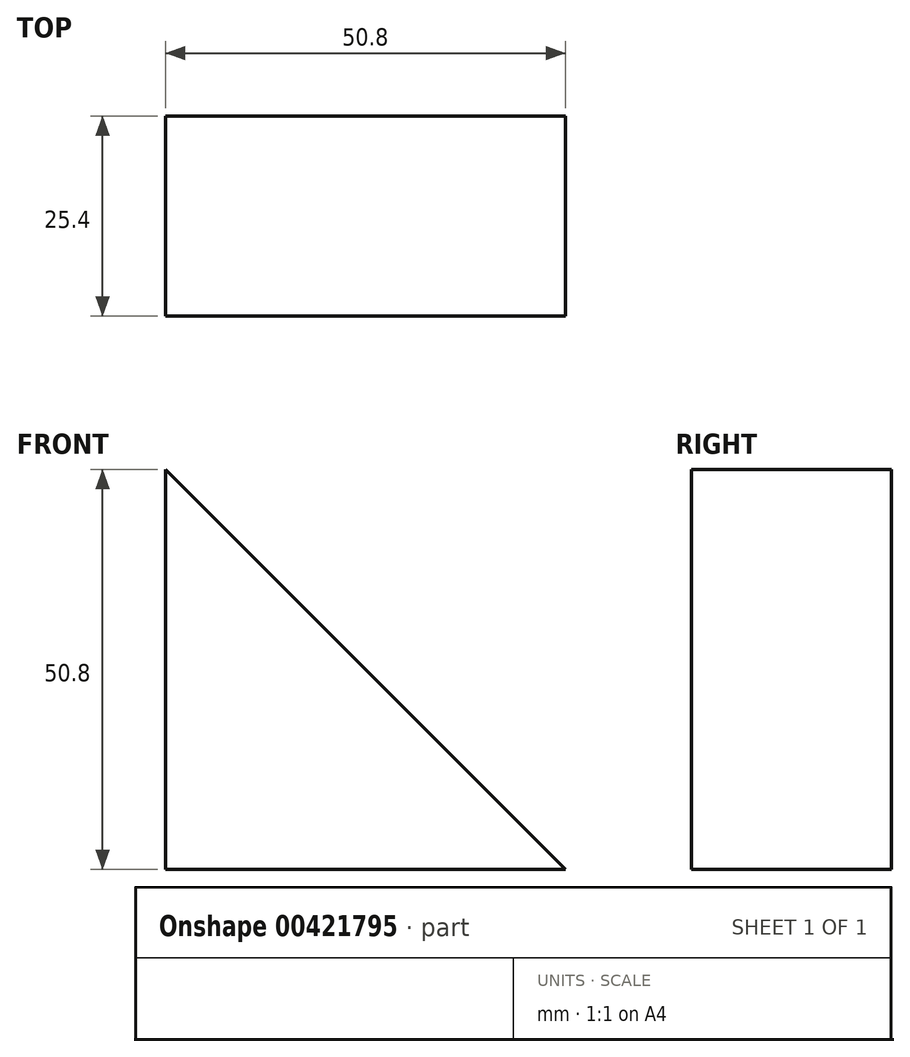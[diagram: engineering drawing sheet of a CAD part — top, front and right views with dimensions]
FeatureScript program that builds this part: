
annotation { "Feature Type Name" : "Feature", "Feature Type Description" : "" }
export const myFeature = defineFeature(function(context is Context, id is Id, definition is map)
    precondition{}
    {
        {
            var Q0;
            Q0=qCreatedBy(makeId("Front.planeOp"),FACE);
            var sketch = newSketch(context, id + "F0", { "sketchPlane" : qUnion([Q0])});
            skLineSegment(sketch, "E0", {"start": v(0, 0) * mm, "end": v(0, 50.8) * mm});
            skLineSegment(sketch, "E1", {"start": v(0, 50.8) * mm, "end": v(0, 0) * mm});
            skLineSegment(sketch, "E2", {"start": v(0, 0) * mm, "end": v(50.8, 0) * mm});
            skLineSegment(sketch, "E3", {"start": v(50.8, 0) * mm, "end": v(0, 50.8) * mm});
            skSolve(sketch);
        }
        {
            var Q0;
            Q0 = qSketchRegion(id + "F0", true);
            extrude(context, id + "F1", {"entities" : qUnion([Q0]), "depth" : 25.4 * mm});
        }
    });
